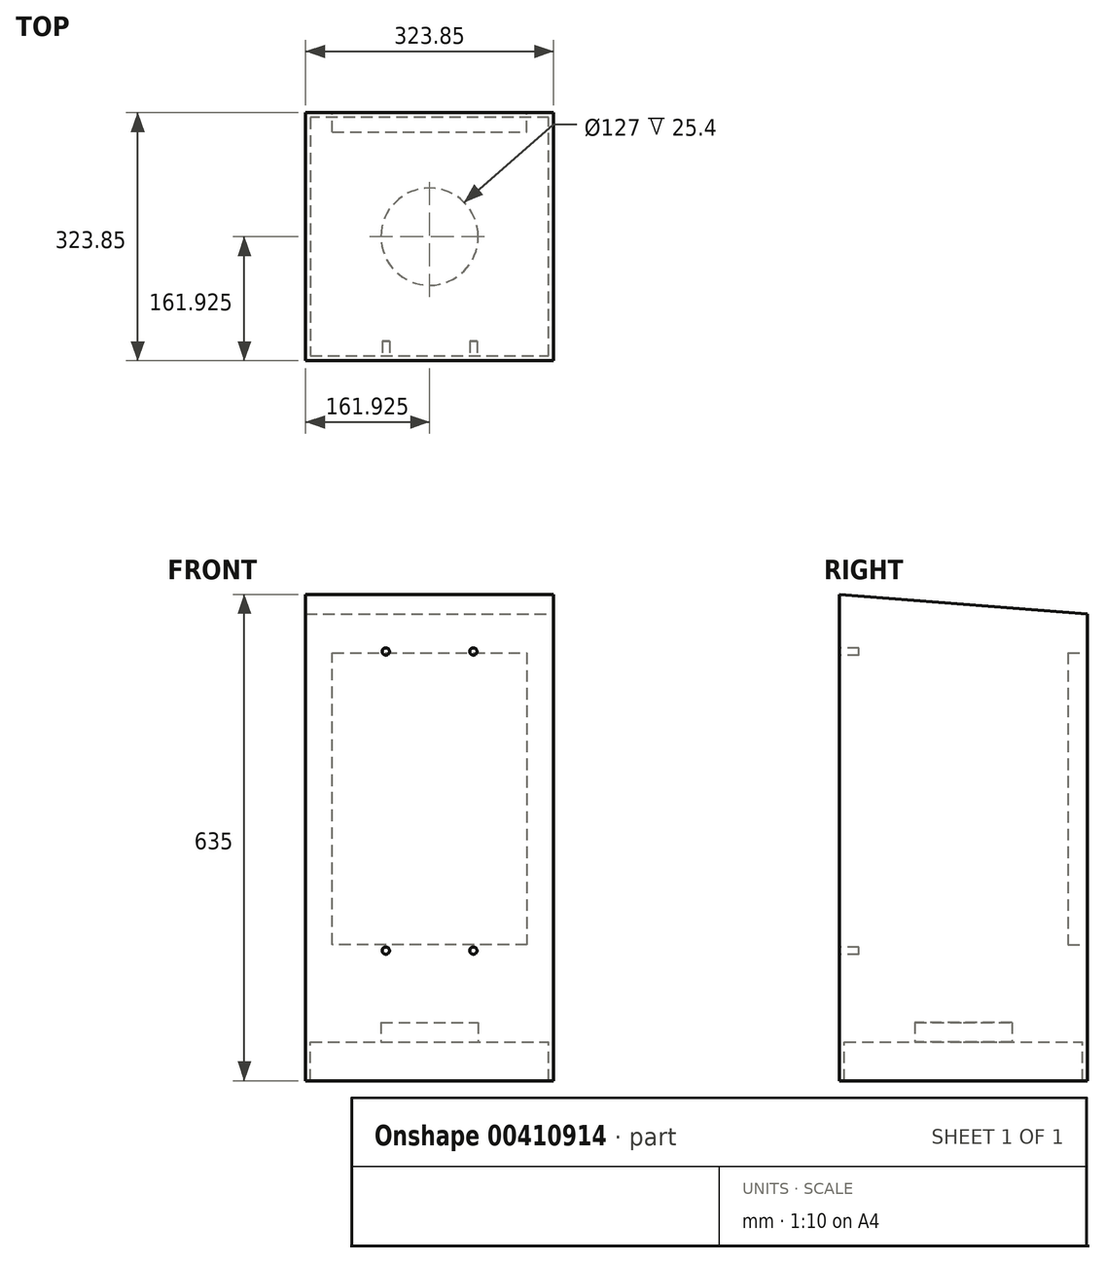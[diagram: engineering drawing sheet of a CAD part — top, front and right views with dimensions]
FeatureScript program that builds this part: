
annotation { "Feature Type Name" : "Feature", "Feature Type Description" : "" }
export const myFeature = defineFeature(function(context is Context, id is Id, definition is map)
    precondition{}
    {
        {
            var Q0;
            Q0=qCreatedBy(makeId("Top.planeOp"),FACE);
            var sketch = newSketch(context, id + "F0", { "sketchPlane" : qUnion([Q0])});
            skLineSegment(sketch, "E0", {"start": v(0, 0) * mm, "end": v(-323.85, 0) * mm});
            skLineSegment(sketch, "E1", {"start": v(-323.85, 0) * mm, "end": v(-323.85, 323.85) * mm});
            skLineSegment(sketch, "E2", {"start": v(-323.85, 323.85) * mm, "end": v(0, 323.85) * mm});
            skLineSegment(sketch, "E3", {"start": v(0, 323.85) * mm, "end": v(0, 0) * mm});
            skSolve(sketch);
        }
        {
            var Q0;
            Q0 = qSketchRegion(id + "F0", true);
            extrude(context, id + "F1", {"entities" : qUnion([Q0]), "depth" : 584.2 * mm});
        }
        {
            var Q0;
            Q0=makeQuery(id+"F1.opExtrude","SWEPT_FACE",FACE,{"disambiguationData":[OSD([sQuery(id+"F0.wireOp",EDGE,"E3")])]});
            var sketch = newSketch(context, id + "F2", { "sketchPlane" : qUnion([Q0])});
            skLineSegment(sketch, "E4", {"start": v(323.85, 558.8) * mm, "end": v(0, 584.2) * mm});
            skLineSegment(sketch, "E5", {"start": v(323.85, 558.8) * mm, "end": v(323.85, 584.2) * mm});
            skLineSegment(sketch, "E6", {"start": v(323.85, 584.2) * mm, "end": v(0, 584.2) * mm});
            skSolve(sketch);
        }
        {
            var Q0;
            Q0=makeQuery(id+"F2.imprint","IMPRINT",FACE,{"disambiguationData":[TD([[makeQuery(id+"F2.imprint","IMPRINT",EDGE,{"derivedFrom":sQuery(id+"F2.wireOp",EDGE,"E4")}),-1.0]])]});
            extrude(context, id + "F3", {"entities" : qUnion([Q0]), "operationType" : NewBodyOperationType.REMOVE, "endBound" : BoundingType.THROUGH_ALL, "oppositeDirection" : true, "depth" : 25.4 * mm});
        }
        {
            var Q0;
            Q0=makeQuery(id+"F1.opExtrude","CAP_FACE",FACE,{"disambiguationData":[OSD([sQuery(id+"F0.wireOp",EDGE,"E0"),sQuery(id+"F0.wireOp",EDGE,"E1"),sQuery(id+"F0.wireOp",EDGE,"E2"),sQuery(id+"F0.wireOp",EDGE,"E3")])],"isStart":true});
            var sketch = newSketch(context, id + "F4", { "sketchPlane" : qUnion([Q0])});
            skLineSegment(sketch, "E7", {"start": v(-161.93, -6.35) * mm, "end": v(-6.35, -6.35) * mm});
            skLineSegment(sketch, "E8", {"start": v(-6.35, -6.35) * mm, "end": v(-6.35, -317.5) * mm});
            skLineSegment(sketch, "E9", {"start": v(-6.35, -317.5) * mm, "end": v(-317.5, -317.5) * mm});
            skLineSegment(sketch, "E10", {"start": v(-317.5, -317.5) * mm, "end": v(-317.5, -6.35) * mm});
            skLineSegment(sketch, "E11", {"start": v(-317.5, -6.35) * mm, "end": v(-161.92, -6.35) * mm});
            skSolve(sketch);
        }
        {
            var Q0;
            Q0=makeQuery(id+"F4.imprint","IMPRINT",FACE,{"disambiguationData":[TD([[makeQuery(id+"F4.imprint","IMPRINT",EDGE,{"derivedFrom":sQuery(id+"F4.wireOp",EDGE,"E7")}),1.0]])]});
            extrude(context, id + "F5", {"entities" : qUnion([Q0]), "operationType" : NewBodyOperationType.ADD, "depth" : 50.8 * mm});
        }
        {
            var Q0;
            {var subQ0=sQuery(id+"F0.wireOp",EDGE,"E0");Q0=makeQuery(id+"F5.boolean.opBoolean","MERGE",FACE,{"derivedFrom":[makeQuery(id+"F1.opExtrude","SWEPT_FACE",FACE,{"disambiguationData":[OSD([subQ0])]}),makeQuery(id+"F5.opExtrude","SWEPT_FACE",FACE,{"disambiguationData":[OSD([subQ0])]})]});}
            var sketch = newSketch(context, id + "F6", { "sketchPlane" : qUnion([Q0])});
            skLineSegment(sketch, "E12", {"start": v(-161.93, -50.8) * mm, "end": v(-161.93, 0) * mm});
            skLineSegment(sketch, "E13", {"start": v(-161.93, 0) * mm, "end": v(-161.93, 509.59) * mm});
            skPoint(sketch, "E14.endSnap0", {"position": v(-161.93, 584.2) * mm});
            skLineSegment(sketch, "E15", {"start": v(-161.93, 509.59) * mm, "end": v(-104.78, 509.59) * mm});
            skLineSegment(sketch, "E16", {"start": v(-161.93, 509.59) * mm, "end": v(-219.08, 509.59) * mm});
            skCircle(sketch, "E17", {"center": v(-104.78, 509.59) * mm, "radius": 4.76 * mm});
            skCircle(sketch, "E18", {"center": v(-219.08, 509.59) * mm, "radius": 4.76 * mm});
            skLineSegment(sketch, "E19", {"start": v(-219.08, 509.59) * mm, "end": v(-219.08, 119.06) * mm});
            skLineSegment(sketch, "E20", {"start": v(-104.78, 509.59) * mm, "end": v(-104.78, 119.06) * mm});
            skCircle(sketch, "E21", {"center": v(-219.08, 119.06) * mm, "radius": 4.76 * mm});
            skCircle(sketch, "E22", {"center": v(-104.78, 119.06) * mm, "radius": 4.76 * mm});
            skSolve(sketch);
        }
        {
            var Q0;
            Q0=makeQuery(id+"F1.opExtrude","CAP_FACE",FACE,{"disambiguationData":[OSD([sQuery(id+"F0.wireOp",EDGE,"E0"),sQuery(id+"F0.wireOp",EDGE,"E1"),sQuery(id+"F0.wireOp",EDGE,"E2"),sQuery(id+"F0.wireOp",EDGE,"E3")])],"isStart":true});
            var sketch = newSketch(context, id + "F7", { "sketchPlane" : qUnion([Q0])});
            skLineSegment(sketch, "E23", {"start": v(-317.5, -6.35) * mm, "end": v(-6.35, -317.5) * mm});
            skCircle(sketch, "E24", {"center": v(-161.92, -161.92) * mm, "radius": 63.5 * mm});
            skSolve(sketch);
        }
        {
            var Q0;
            Q0 = qSketchRegion(id + "F7", true);
            extrude(context, id + "F8", {"entities" : qUnion([Q0]), "operationType" : NewBodyOperationType.REMOVE, "oppositeDirection" : true, "depth" : 25.4 * mm});
        }
        {
            var Q0;
            Q0 = qSketchRegion(id + "F6", true);
            extrude(context, id + "F9", {"entities" : qUnion([Q0]), "operationType" : NewBodyOperationType.REMOVE, "oppositeDirection" : true, "depth" : 25.4 * mm});
        }
        {
            var Q0;
            Q0 = qSketchRegion(id + "F6", true);
            extrude(context, id + "F10", {"entities" : qUnion([Q0]), "operationType" : NewBodyOperationType.REMOVE, "oppositeDirection" : true, "depth" : 25.4 * mm});
        }
        {
            var Q0;
            {var subQ0=sQuery(id+"F0.wireOp",EDGE,"E2");Q0=makeQuery(id+"F5.boolean.opBoolean","MERGE",FACE,{"derivedFrom":[makeQuery(id+"F1.opExtrude","SWEPT_FACE",FACE,{"disambiguationData":[OSD([subQ0])]}),makeQuery(id+"F5.opExtrude","SWEPT_FACE",FACE,{"disambiguationData":[OSD([subQ0])]})]});}
            var sketch = newSketch(context, id + "F11", { "sketchPlane" : qUnion([Q0])});
            skLineSegment(sketch, "E25", {"start": v(161.92, 508) * mm, "end": v(34.93, 508) * mm});
            skLineSegment(sketch, "E26", {"start": v(34.93, 508) * mm, "end": v(34.93, 127) * mm});
            skLineSegment(sketch, "E27", {"start": v(34.93, 127) * mm, "end": v(288.93, 127) * mm});
            skLineSegment(sketch, "E28", {"start": v(288.93, 127) * mm, "end": v(288.93, 508) * mm});
            skLineSegment(sketch, "E29", {"start": v(288.93, 508) * mm, "end": v(161.92, 508) * mm});
            skSolve(sketch);
        }
        {
            var Q0;
            Q0 = qSketchRegion(id + "F11", true);
            extrude(context, id + "F12", {"entities" : qUnion([Q0]), "operationType" : NewBodyOperationType.REMOVE, "oppositeDirection" : true, "depth" : 25.4 * mm});
        }
    });
